# Revit family: FP-Revit19-FC1260H1-Cabinet-90002789A
name_source: partatom
category: Specialty Equipment
units: mm (PartAtom-declared; Revit-internal decimal feet)

## family parameters
Always vertical = Yes
Cut with Voids When Loaded = Yes
Part Type = Normal
Room Calculation Point = No
Round Connector Dimension = Use Diameter
Shared = No
Work Plane-Based = No

## types (2) — shared parameters
Cavity - Depth = 700 mm  [stored 2.29659 ft]
Cavity - Width = 640 mm  [stored 2.09974 ft]
Chassis - Depth = 614 mm  [stored 2.01444 ft]
Chassis - Height = 1864 mm  [stored 6.11549 ft]
Chassis - Width = 600 mm  [stored 1.9685 ft]
Connector Description - Electrical = 220 – 240 V, 50 Hz, 10 A circuit
Description = Fabric Care Cabinet
Manufacturer = Fisher & Paykel Appliances Ltd
Material - Body = Fisher & Paykel - Grey
Material - Display Panel = Fisher & Paykel - Black
Material - Trim = Fisher & Paykel - Silver Anodized
Product - Depth = 667 mm
Product - Height (1897mm - 1907mm) = 1900 mm  [stored 6.2336 ft]
Product - Width = 600 mm  [stored 1.9685 ft]
Visibility - Clearance Required = Yes
zero-valued in all types: Default Elevation

## per-type parameters (varying)
| type | Cavity - Height (1917 - 1927) | Material - Front | Model |
| FC1260H1 | 1917 mm | Fisher & Paykel - White | FC1260H1 |
| FC1260HG1 | 1920 mm  [stored 6.29921 ft] | Fisher & Paykel - Grey, Charcoal | FC1260G1 |

note: [stored X ft] marks values corroborated as IEEE doubles in the binary element streams (Revit-internal decimal feet)

## geometry (parser evidence)
native form markers: Sweep x2
no freeform markers — native parametric forms only
